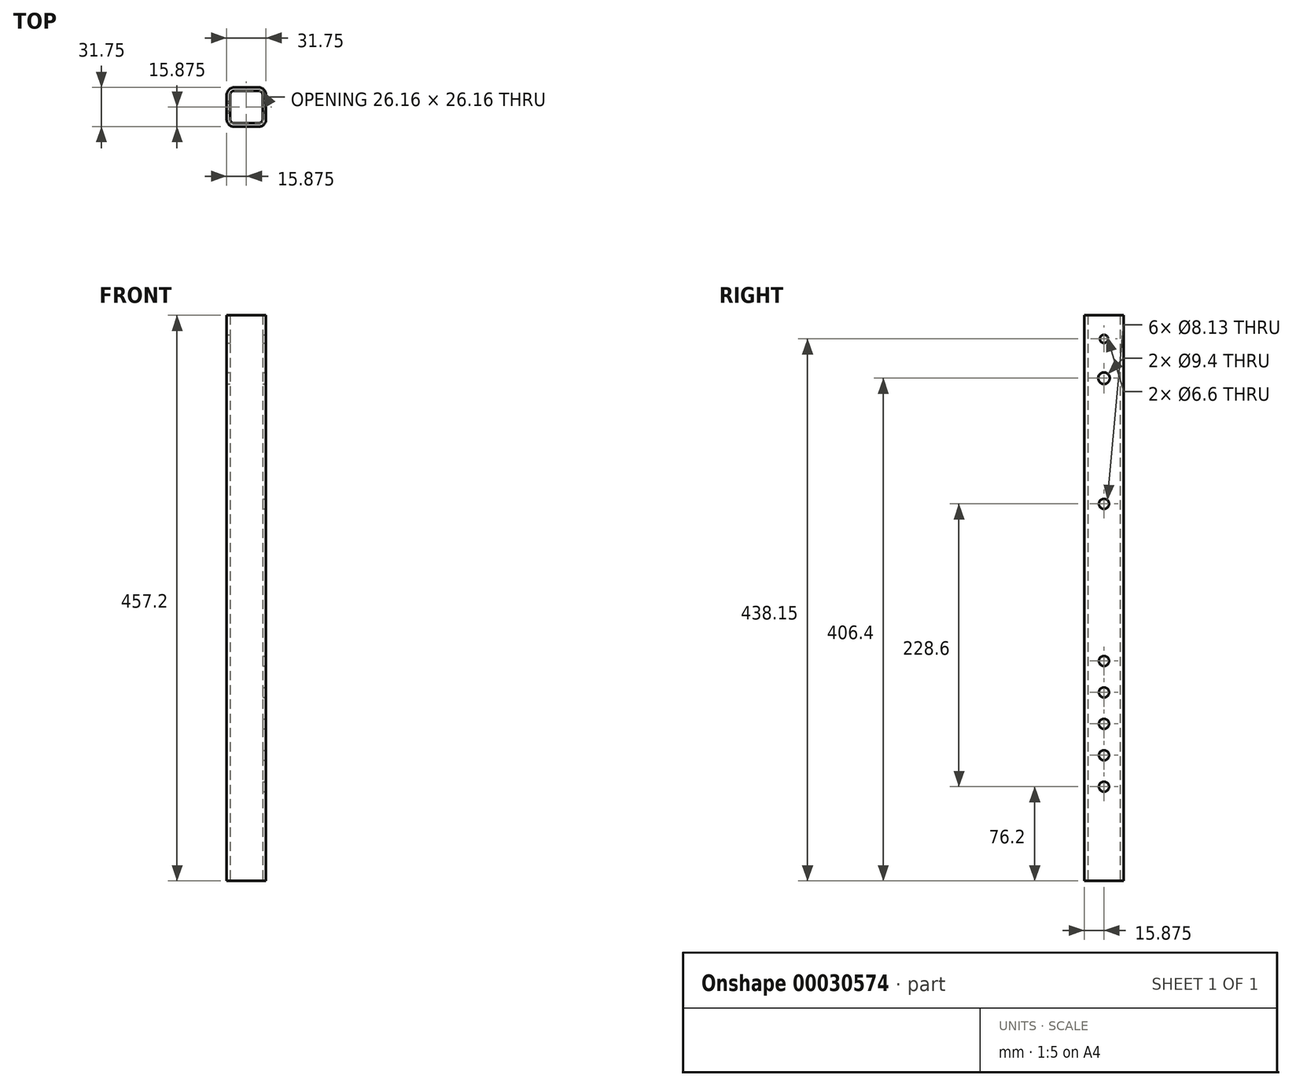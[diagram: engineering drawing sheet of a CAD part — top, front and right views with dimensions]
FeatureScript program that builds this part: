
annotation { "Feature Type Name" : "Feature", "Feature Type Description" : "" }
export const myFeature = defineFeature(function(context is Context, id is Id, definition is map)
    precondition{}
    {
        {
            var Q0;
            Q0=qCreatedBy(makeId("Top.planeOp"),FACE);
            var sketch = newSketch(context, id + "F0", { "sketchPlane" : qUnion([Q0])});
            skLineSegment(sketch, "E0.bottom", {"start": v(5.97, 0) * mm, "end": v(25.78, 0) * mm});
            skLineSegment(sketch, "E0.top", {"start": v(5.97, 31.75) * mm, "end": v(25.78, 31.75) * mm});
            skLineSegment(sketch, "E0.left", {"start": v(0, 5.97) * mm, "end": v(0, 25.78) * mm});
            skLineSegment(sketch, "E0.right", {"start": v(31.75, 5.97) * mm, "end": v(31.75, 25.78) * mm});
            skLineSegment(sketch, "E1.0", {"start": v(2.8, 5.97) * mm, "end": v(2.8, 25.78) * mm});
            skLineSegment(sketch, "E1.1", {"start": v(5.97, 2.8) * mm, "end": v(25.78, 2.8) * mm});
            skLineSegment(sketch, "E1.2", {"start": v(28.96, 5.97) * mm, "end": v(28.96, 25.78) * mm});
            skLineSegment(sketch, "E1.3", {"start": v(5.97, 28.96) * mm, "end": v(25.78, 28.96) * mm});
            skPoint(sketch, "E2.visualSharp", {"position": v(2.8, 28.96) * mm});
            skArc(sketch, "E2.filletArc", {"start": v(5.97, 28.96) * mm, "mid": v(3.72, 28.03) * mm, "end": v(2.8, 25.78) * mm});
            skPoint(sketch, "E3.visualSharp", {"position": v(28.96, 28.96) * mm});
            skArc(sketch, "E3.filletArc", {"start": v(28.96, 25.78) * mm, "mid": v(28.03, 28.03) * mm, "end": v(25.78, 28.96) * mm});
            skPoint(sketch, "E4.visualSharp", {"position": v(2.8, 2.8) * mm});
            skArc(sketch, "E4.filletArc", {"start": v(2.8, 5.97) * mm, "mid": v(3.72, 3.72) * mm, "end": v(5.97, 2.8) * mm});
            skPoint(sketch, "E5.visualSharp", {"position": v(28.96, 2.8) * mm});
            skArc(sketch, "E5.filletArc", {"start": v(25.78, 2.8) * mm, "mid": v(28.03, 3.72) * mm, "end": v(28.96, 5.97) * mm});
            skPoint(sketch, "E6.visualSharp", {"position": v(0, 31.75) * mm});
            skArc(sketch, "E6.filletArc", {"start": v(5.97, 31.75) * mm, "mid": v(1.75, 30) * mm, "end": v(0, 25.78) * mm});
            skPoint(sketch, "E7.visualSharp", {"position": v(31.75, 31.75) * mm});
            skArc(sketch, "E7.filletArc", {"start": v(31.75, 25.78) * mm, "mid": v(30, 30) * mm, "end": v(25.78, 31.75) * mm});
            skPoint(sketch, "E8.visualSharp", {"position": v(31.75, 0) * mm});
            skArc(sketch, "E8.filletArc", {"start": v(25.78, 0) * mm, "mid": v(30, 1.75) * mm, "end": v(31.75, 5.97) * mm});
            skPoint(sketch, "E9.visualSharp", {"position": v(0, 0) * mm});
            skArc(sketch, "E9.filletArc", {"start": v(0, 5.97) * mm, "mid": v(1.75, 1.75) * mm, "end": v(5.97, 0) * mm});
            skSolve(sketch);
        }
        {
            var Q0;
            Q0 = qSketchRegion(id + "F0", true);
            extrude(context, id + "F1", {"entities" : qUnion([Q0]), "depth" : 457.2 * mm});
        }
        {
            var Q0;
            Q0=makeQuery(id+"F1.opExtrude","SWEPT_FACE",FACE,{"disambiguationData":[OSD([sQuery(id+"F0.wireOp",EDGE,"E0.right")])]});
            var sketch = newSketch(context, id + "F2", { "sketchPlane" : qUnion([Q0])});
            skLineSegment(sketch, "E10", {"start": v(15.87, 457.2) * mm, "end": v(15.87, 438.15) * mm, "construction": true});
            skCircle(sketch, "E11", {"center": v(15.87, 438.15) * mm, "radius": 3.3 * mm});
            skLineSegment(sketch, "E12", {"start": v(15.87, 438.15) * mm, "end": v(15.87, 406.4) * mm, "construction": true});
            skCircle(sketch, "E13", {"center": v(15.88, 406.4) * mm, "radius": 4.7 * mm});
            skSolve(sketch);
        }
        {
            var Q0;
            Q0 = qSketchRegion(id + "F2", true);
            extrude(context, id + "F3", {"entities" : qUnion([Q0]), "operationType" : NewBodyOperationType.REMOVE, "endBound" : BoundingType.THROUGH_ALL, "oppositeDirection" : true, "depth" : 25.4 * mm});
        }
        {
            var Q0;
            Q0=makeQuery(id+"F1.opExtrude","SWEPT_FACE",FACE,{"disambiguationData":[OSD([sQuery(id+"F0.wireOp",EDGE,"E0.right")])]});
            var sketch = newSketch(context, id + "F4", { "sketchPlane" : qUnion([Q0])});
            skLineSegment(sketch, "E14", {"start": v(15.87, 0) * mm, "end": v(15.87, 76.2) * mm, "construction": true});
            skCircle(sketch, "E15", {"center": v(15.87, 76.2) * mm, "radius": 4.06 * mm});
            skCircle(sketch, "E16.0.1.0", {"center": v(15.87, 101.6) * mm, "radius": 4.06 * mm});
            skCircle(sketch, "E16.0.2.0", {"center": v(15.87, 127) * mm, "radius": 4.06 * mm});
            skCircle(sketch, "E16.0.3.0", {"center": v(15.87, 152.4) * mm, "radius": 4.06 * mm});
            skCircle(sketch, "E16.0.4.0", {"center": v(15.87, 177.8) * mm, "radius": 4.06 * mm});
            skLineSegment(sketch, "E16.direction1", {"start": v(15.87, 76.2) * mm, "end": v(41.27, 76.2) * mm, "construction": true});
            skLineSegment(sketch, "E16.direction2", {"start": v(15.87, 76.2) * mm, "end": v(15.87, 101.6) * mm, "construction": true});
            skLineSegment(sketch, "E17", {"start": v(15.87, 177.8) * mm, "end": v(15.87, 304.8) * mm, "construction": true});
            skCircle(sketch, "E18", {"center": v(15.88, 304.8) * mm, "radius": 4.06 * mm});
            skSolve(sketch);
        }
        {
            var Q0;
            Q0 = qSketchRegion(id + "F4", true);
            extrude(context, id + "F5", {"entities" : qUnion([Q0]), "operationType" : NewBodyOperationType.REMOVE, "endBound" : BoundingType.UP_TO_NEXT, "oppositeDirection" : true, "depth" : 25.4 * mm});
        }
    });
